# Revit family: Shower-Valves_and_Controls-KOHLER-MasterShower-K-2974
name_source: partatom
category: Plumbing Fixtures
revit_build: Autodesk Revit 2015 (Build: 20140606_1530(x64)
units: mm (PartAtom-declared; Revit-internal decimal feet)

## types (1)
- 1/2 Inch volume control valve
    ADA Compliant = No
    Assembly Code = D2020
    CW Connection = No
    Cold Water Inlet = Cold Water Inlet
    Date Modified = 11/13/2018
    Default Elevation = 36"
    Description = 1/2 inch volume control valve
    Finish = Kohler-Metal-Brass
    Flow Rate = 10 GPM
    HW Connection = Yes
    Height = 3"
    Hot Water Inlet = Hot Water Inlet
    Length = 2 7/16"
    Manufacturer = KOHLER Co.
    MasterFormat 1995 = 154300
    MasterFormat 2004 = 22.11.00
    Material = Brass Construction
    Model = K-2974-K-NA
    Pressure = 45.00 psi
    Product Documentation Link = http://www.us.kohler.com
    Product Name = MasterShower
    Product Page URL = http://www.us.kohler.com
    Tempered Water Outlet 1 = Tempered Water Inlet
    Tempered Water Outlet 2 = Tempered Water Outlet
    Type = 1
    URL = https://www.us.kohler.com
    Vent Connection = No
    Waste Connection = No
    Waste Water Outlet = Waste Water Outlet
    Width = 1 3/4"

## geometry (parser evidence)
native form markers: Sweep x4
no freeform markers — native parametric forms only
